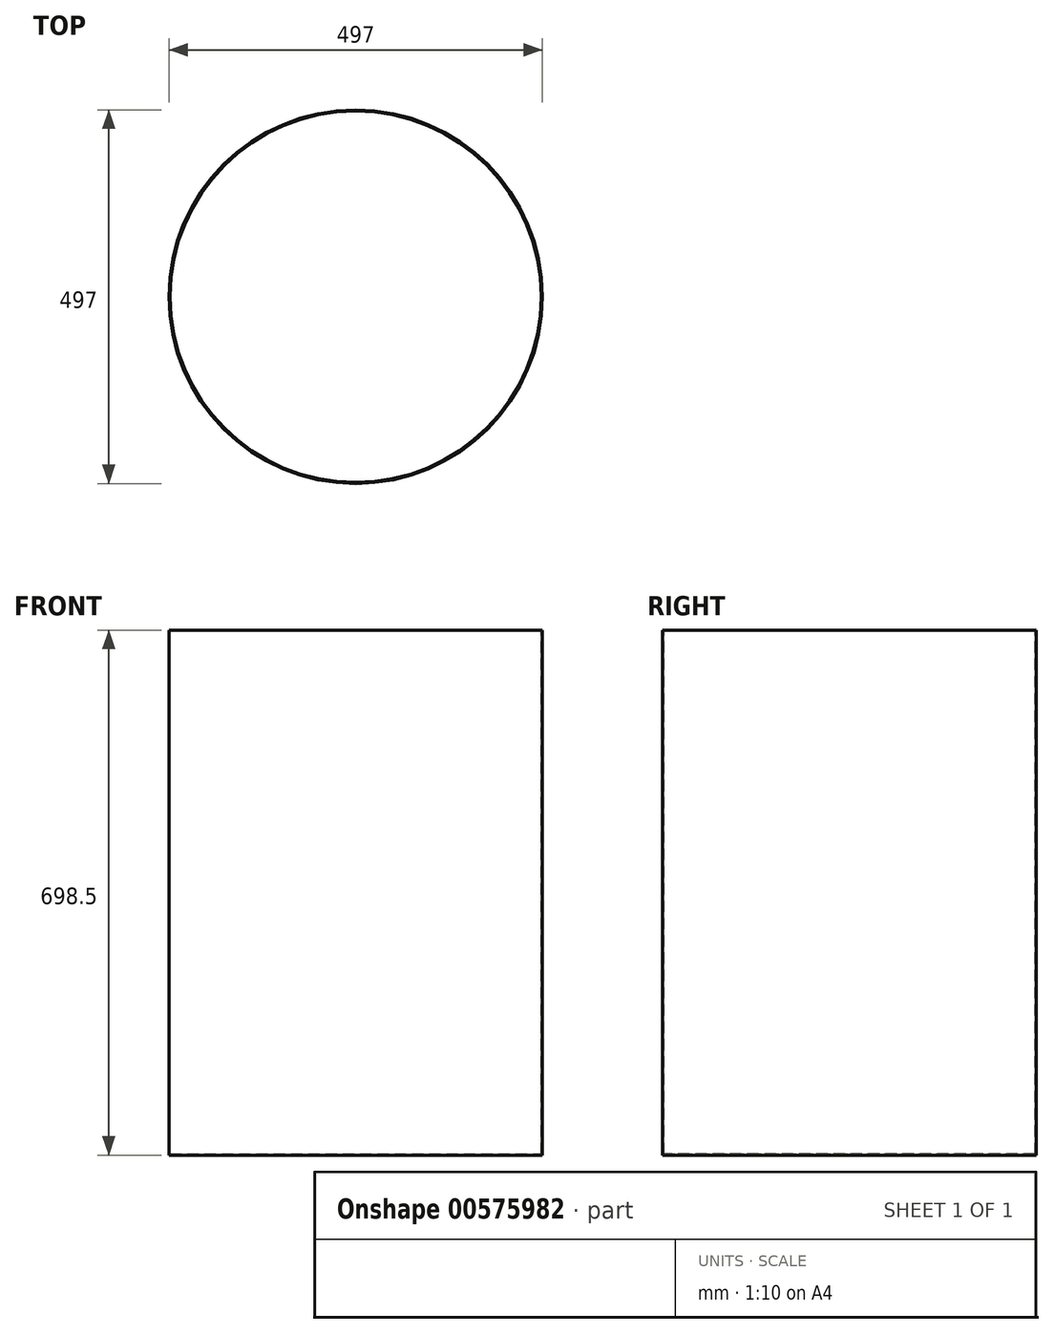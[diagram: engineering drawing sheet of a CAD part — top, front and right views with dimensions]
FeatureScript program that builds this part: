
annotation { "Feature Type Name" : "Feature", "Feature Type Description" : "" }
export const myFeature = defineFeature(function(context is Context, id is Id, definition is map)
    precondition{}
    {
        {
            var Q0;
            Q0=qCreatedBy(makeId("Right.planeOp"),FACE);
            var sketch = newSketch(context, id + "F0", { "sketchPlane" : qUnion([Q0])});
            skLineSegment(sketch, "E0", {"start": v(0, 192.5) * mm, "end": v(0, 109.12) * mm, "construction": true});
            skLineSegment(sketch, "E1", {"start": v(-248.5, 149.12) * mm, "end": v(-248.5, 109.12) * mm});
            skLineSegment(sketch, "E2", {"start": v(0, 0) * mm, "end": v(257.23, 0) * mm, "construction": true});
            skLineSegment(sketch, "E3", {"start": v(-248.5, 149.12) * mm, "end": v(-248.5, 807.62) * mm});
            skLineSegment(sketch, "E4", {"start": v(-248.5, 807.62) * mm, "end": v(0, 807.62) * mm});
            skLineSegment(sketch, "E5", {"start": v(0, 807.62) * mm, "end": v(0, 109.12) * mm});
            skLineSegment(sketch, "E6", {"start": v(-248.5, 109.12) * mm, "end": v(0, 109.12) * mm});
            skLineSegment(sketch, "E7.trimOffspring", {"start": v(0, 0) * mm, "end": v(0, -214.32) * mm, "construction": true});
            skSolve(sketch);
        }
        {
            var Q0;
            Q0=makeQuery(id+"F0.imprint","IMPRINT",FACE,{"disambiguationData":[TD([[makeQuery(id+"F0.imprint","IMPRINT",EDGE,{"derivedFrom":sQuery(id+"F0.wireOp",EDGE,"E1")}),1.0]])]});
            var Q1;
            Q1=sQuery(id+"F0.wireOp",EDGE,"E7.trimOffspring");
            revolve(context, id + "F1", {"surfaceOperationType" : NewSurfaceOperationType.NEW, "entities" : qUnion([Q0]), "axis" : qUnion([Q1]), "revolveType" : RevolveType.FULL});
        }
        {
            var Q0;
            Q0=makeQuery(id+"F1.opRevolve","SWEPT_FACE",FACE,{"disambiguationData":[OSD([sQuery(id+"F0.wireOp",EDGE,"E4")])]});
            shell(context, id + "F2", {"entities" : qUnion([Q0]), "thickness" : 1.5 * mm});
        }
    });
